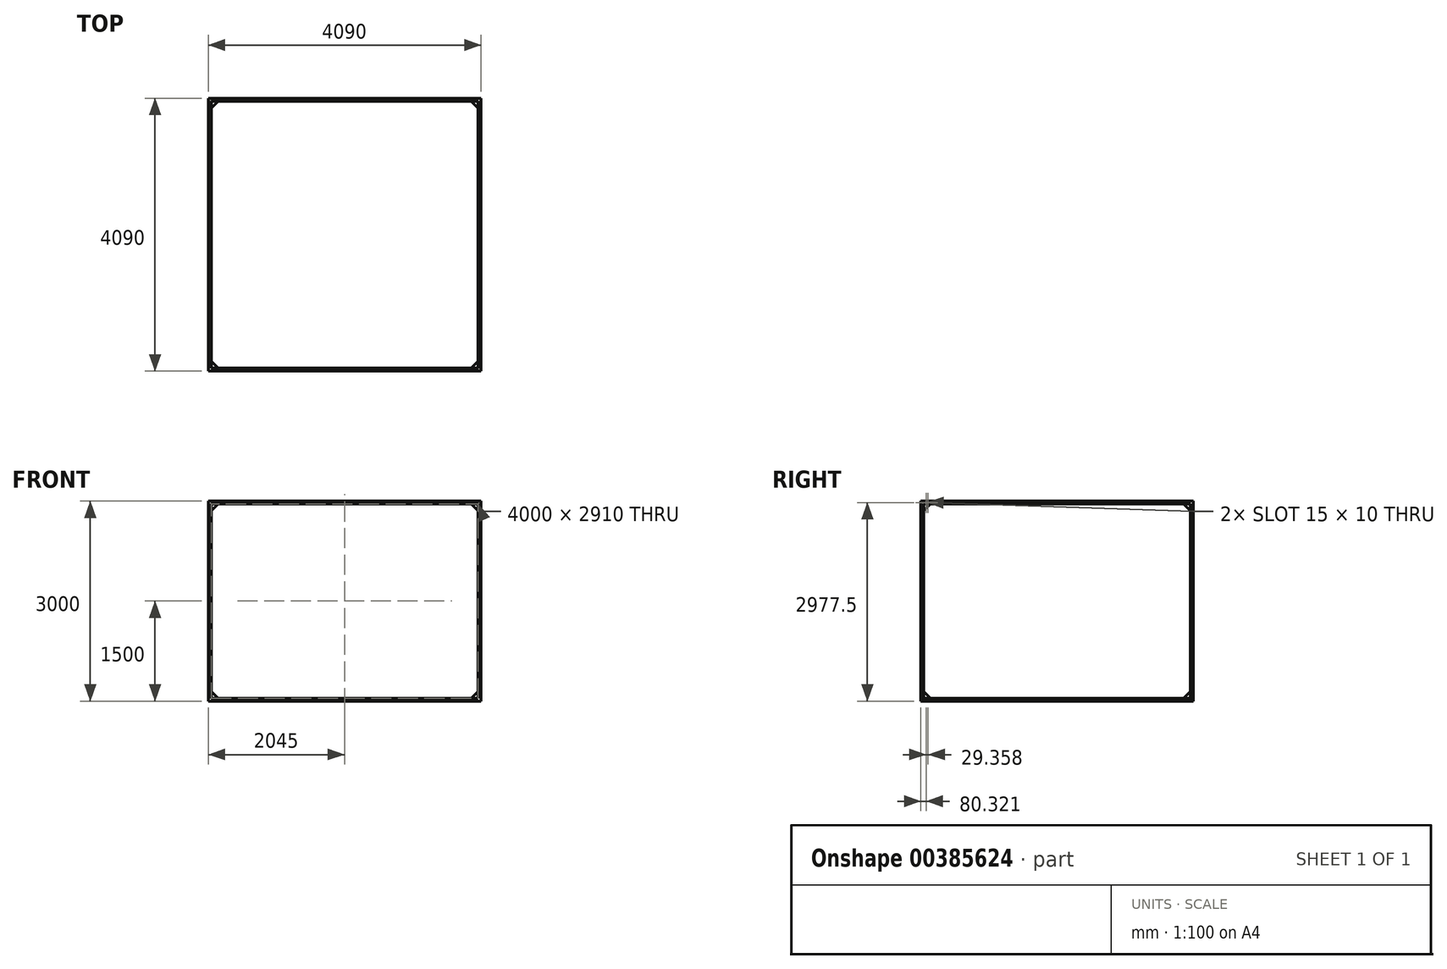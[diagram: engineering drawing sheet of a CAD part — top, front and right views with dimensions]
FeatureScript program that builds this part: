
annotation { "Feature Type Name" : "Feature", "Feature Type Description" : "" }
export const myFeature = defineFeature(function(context is Context, id is Id, definition is map)
    precondition{}
    {
        {
            var Q0;
            Q0=qCreatedBy(makeId("Front.planeOp"),FACE);
            var sketch = newSketch(context, id + "F0", { "sketchPlane" : qUnion([Q0])});
            skLineSegment(sketch, "E0.bottom", {"start": v(-214.64, 1461.4) * mm, "end": v(-169.64, 1461.4) * mm});
            skLineSegment(sketch, "E0.top", {"start": v(-214.64, -1538.6) * mm, "end": v(-169.64, -1538.6) * mm});
            skLineSegment(sketch, "E0.left", {"start": v(-214.64, 1461.4) * mm, "end": v(-214.64, -1538.6) * mm});
            skLineSegment(sketch, "E0.right", {"start": v(-169.64, 1461.4) * mm, "end": v(-169.64, -1538.6) * mm});
            skLineSegment(sketch, "E1", {"start": v(1830.36, 1828.03) * mm, "end": v(1830.36, -2580.42) * mm, "construction": true});
            skLineSegment(sketch, "E2.MirrorCS", {"start": v(3830.36, 1461.4) * mm, "end": v(3830.36, -1538.6) * mm});
            skLineSegment(sketch, "E3.MirrorCS", {"start": v(3875.36, 1461.4) * mm, "end": v(3875.36, -1538.6) * mm});
            skLineSegment(sketch, "E4.MirrorCS", {"start": v(3875.36, 1461.4) * mm, "end": v(3830.36, 1461.4) * mm});
            skLineSegment(sketch, "E5.MirrorCS", {"start": v(3875.36, -1538.6) * mm, "end": v(3830.36, -1538.6) * mm});
            skLineSegment(sketch, "E6.bottom", {"start": v(-169.64, 1461.4) * mm, "end": v(3830.36, 1461.4) * mm});
            skLineSegment(sketch, "E6.top", {"start": v(-169.64, 1416.4) * mm, "end": v(3830.36, 1416.4) * mm});
            skLineSegment(sketch, "E6.left", {"start": v(-169.64, 1461.4) * mm, "end": v(-169.64, 1416.4) * mm});
            skLineSegment(sketch, "E6.right", {"start": v(3830.36, 1461.4) * mm, "end": v(3830.36, 1416.4) * mm});
            skLineSegment(sketch, "E7.bottom", {"start": v(-169.64, -1538.6) * mm, "end": v(3830.36, -1538.6) * mm});
            skLineSegment(sketch, "E7.top", {"start": v(-169.64, -1493.6) * mm, "end": v(3830.36, -1493.6) * mm});
            skLineSegment(sketch, "E7.left", {"start": v(-169.64, -1538.6) * mm, "end": v(-169.64, -1493.6) * mm});
            skLineSegment(sketch, "E7.right", {"start": v(3830.36, -1538.6) * mm, "end": v(3830.36, -1493.6) * mm});
            skSolve(sketch);
        }
        {
            var Q0;
            {var subQ4=sQuery(id+"F0.wireOp",EDGE,"E0.bottom");Q0=makeQuery(id+"F0.imprint","IMPRINT",FACE,{"disambiguationData":[TD([[makeQuery(id+"F0.imprint","IMPRINT",EDGE,{"derivedFrom":subQ4}),-1.0]])]});}
            var Q1;
            Q1=makeQuery(id+"F0.imprint","IMPRINT",FACE,{"disambiguationData":[TD([[makeQuery(id+"F0.imprint","IMPRINT",EDGE,{"derivedFrom":sQuery(id+"F0.wireOp",EDGE,"E3.MirrorCS")}),-1.0]])]});
            var Q2;
            {var subQ0=sQuery(id+"F0.wireOp",EDGE,"E6.bottom");Q2=makeQuery(id+"F0.imprint","IMPRINT",FACE,{"disambiguationData":[TD([[makeQuery(id+"F0.imprint","IMPRINT",EDGE,{"derivedFrom":subQ0}),-1.0]])]});}
            var Q3;
            {var subQ0=sQuery(id+"F0.wireOp",EDGE,"E7.bottom");Q3=makeQuery(id+"F0.imprint","IMPRINT",FACE,{"disambiguationData":[TD([[makeQuery(id+"F0.imprint","IMPRINT",EDGE,{"derivedFrom":subQ0}),1.0]])]});}
            extrude(context, id + "F1", {"entities" : qUnion([Q0, Q1, Q2, Q3]), "depth" : 45 * mm});
        }
        {
            var Q0;
            Q0=makeQuery(id+"F1.opExtrude","CAP_FACE",FACE,{"disambiguationData":[OSD([sQuery(id+"F0.wireOp",EDGE,"E0.bottom"),sQuery(id+"F0.wireOp",EDGE,"E0.top"),sQuery(id+"F0.wireOp",EDGE,"E0.left"),sQuery(id+"F0.wireOp",EDGE,"E0.right"),sQuery(id+"F0.wireOp",EDGE,"E2.MirrorCS"),sQuery(id+"F0.wireOp",EDGE,"E3.MirrorCS"),sQuery(id+"F0.wireOp",EDGE,"E4.MirrorCS"),sQuery(id+"F0.wireOp",EDGE,"E5.MirrorCS"),sQuery(id+"F0.wireOp",EDGE,"E6.bottom"),sQuery(id+"F0.wireOp",EDGE,"E6.top"),sQuery(id+"F0.wireOp",EDGE,"E7.bottom"),sQuery(id+"F0.wireOp",EDGE,"E7.top")])],"isStart":false});
            cPlane(context, id + "F2", {"entities" : qUnion([Q0]), "cplaneType" : CPlaneType.OFFSET, "offset" : 2000 * mm, "width" : 150 * mm, "height" : 150 * mm});
        }
        {
            var Q0;
            Q0=makeQuery(id+"F1.opExtrude","SWEPT_BODY",BODY,{"disambiguationData":[OSD([sQuery(id+"F0.wireOp",EDGE,"E0.bottom"),sQuery(id+"F0.wireOp",EDGE,"E0.top"),sQuery(id+"F0.wireOp",EDGE,"E0.left"),sQuery(id+"F0.wireOp",EDGE,"E0.right"),sQuery(id+"F0.wireOp",EDGE,"E2.MirrorCS"),sQuery(id+"F0.wireOp",EDGE,"E3.MirrorCS"),sQuery(id+"F0.wireOp",EDGE,"E4.MirrorCS"),sQuery(id+"F0.wireOp",EDGE,"E5.MirrorCS"),sQuery(id+"F0.wireOp",EDGE,"E6.bottom"),sQuery(id+"F0.wireOp",EDGE,"E6.top"),sQuery(id+"F0.wireOp",EDGE,"E7.bottom"),sQuery(id+"F0.wireOp",EDGE,"E7.top")])]});
            var Q1;
            Q1=qCreatedBy(id+"F2.planeOp",FACE);
            mirror(context, id + "F3", {"entities" : qUnion([Q0]), "mirrorPlane" : qUnion([Q1])});
        }
        {
            var Q0;
            Q0=makeQuery(id+"F3.opPattern","COPY",FACE,{"derivedFrom":makeQuery(id+"F1.opExtrude","SWEPT_FACE",FACE,{"disambiguationData":[OSD([sQuery(id+"F0.wireOp",EDGE,"E0.bottom"),sQuery(id+"F0.wireOp",EDGE,"E4.MirrorCS"),sQuery(id+"F0.wireOp",EDGE,"E6.bottom")])]}),"instanceName":"1"});
            var sketch = newSketch(context, id + "F4", { "sketchPlane" : qUnion([Q0])});
            skLineSegment(sketch, "E8.bottom", {"start": v(-214.64, -4045) * mm, "end": v(-169.64, -4045) * mm});
            skLineSegment(sketch, "E8.top", {"start": v(-214.64, -45) * mm, "end": v(-169.64, -45) * mm});
            skLineSegment(sketch, "E8.left", {"start": v(-214.64, -4045) * mm, "end": v(-214.64, -45) * mm});
            skLineSegment(sketch, "E8.right", {"start": v(-169.64, -4045) * mm, "end": v(-169.64, -45) * mm});
            skLineSegment(sketch, "E9.0.0", {"start": v(3875.36, 0) * mm, "end": v(-214.64, 0) * mm});
            skLineSegment(sketch, "E9.0.1", {"start": v(-214.64, 0) * mm, "end": v(-214.64, -45) * mm});
            skLineSegment(sketch, "E9.0.2", {"start": v(-214.64, -45) * mm, "end": v(3875.36, -45) * mm});
            skLineSegment(sketch, "E9.0.3", {"start": v(3875.36, -45) * mm, "end": v(3875.36, 0) * mm});
            skLineSegment(sketch, "E10", {"start": v(1830.36, -4045) * mm, "end": v(1830.36, 1032.85) * mm, "construction": true});
            skLineSegment(sketch, "E11.MirrorCS", {"start": v(3830.36, -4045) * mm, "end": v(3830.36, -45) * mm});
            skLineSegment(sketch, "E12.MirrorCS", {"start": v(3875.36, -4045) * mm, "end": v(3875.36, -45) * mm});
            skSolve(sketch);
        }
        {
            var Q0;
            {var subQ2=sQuery(id+"F4.wireOp",EDGE,"E11.MirrorCS");Q0=makeQuery(id+"F4.imprint","IMPRINT",FACE,{"disambiguationData":[TD([[makeQuery(id+"F4.imprint","IMPRINT",EDGE,{"derivedFrom":subQ2}),-1.0]])]});}
            var Q1;
            Q1=makeQuery(id+"F4.imprint","IMPRINT",FACE,{"disambiguationData":[TD([[makeQuery(id+"F4.imprint","IMPRINT",EDGE,{"derivedFrom":sQuery(id+"F4.wireOp",EDGE,"E8.bottom")}),1.0]])]});
            extrude(context, id + "F5", {"entities" : qUnion([Q0, Q1]), "operationType" : NewBodyOperationType.ADD, "oppositeDirection" : true, "depth" : 45 * mm});
        }
        {
            var Q0;
            {var subQ0=makeQuery(id+"F1.opExtrude","SWEPT_FACE",FACE,{"disambiguationData":[OSD([sQuery(id+"F0.wireOp",EDGE,"E0.left")])]});Q0=makeQuery(id+"F5.boolean.opBoolean","MERGE",FACE,{"derivedFrom":[subQ0,makeQuery(id+"F3.opPattern","COPY",FACE,{"derivedFrom":subQ0,"instanceName":"1"}),makeQuery(id+"F5.opExtrude","SWEPT_FACE",FACE,{"disambiguationData":[OSD([sQuery(id+"F4.wireOp",EDGE,"E8.left")])]})]});}
            var sketch = newSketch(context, id + "F6", { "sketchPlane" : qUnion([Q0])});
            skLineSegment(sketch, "E13.0.0", {"start": v(0, 1461.4) * mm, "end": v(0, -1538.6) * mm});
            skLineSegment(sketch, "E13.0.1", {"start": v(0, -1538.6) * mm, "end": v(45, -1538.6) * mm});
            skLineSegment(sketch, "E13.0.2", {"start": v(45, -1538.6) * mm, "end": v(45, 1416.4) * mm});
            skLineSegment(sketch, "E13.0.3", {"start": v(45, 1416.4) * mm, "end": v(4045, 1416.4) * mm});
            skLineSegment(sketch, "E13.0.4", {"start": v(4045, 1416.4) * mm, "end": v(4045, -1538.6) * mm});
            skLineSegment(sketch, "E13.0.5", {"start": v(4045, -1538.6) * mm, "end": v(4090, -1538.6) * mm});
            skLineSegment(sketch, "E13.0.6", {"start": v(4090, -1538.6) * mm, "end": v(4090, 1461.4) * mm});
            skLineSegment(sketch, "E13.0.7", {"start": v(4090, 1461.4) * mm, "end": v(0, 1461.4) * mm});
            skLineSegment(sketch, "E14.bottom", {"start": v(4045, -1538.6) * mm, "end": v(45, -1538.6) * mm});
            skLineSegment(sketch, "E14.top", {"start": v(4045, -1493.6) * mm, "end": v(45, -1493.6) * mm});
            skLineSegment(sketch, "E14.left", {"start": v(4045, -1538.6) * mm, "end": v(4045, -1493.6) * mm});
            skLineSegment(sketch, "E14.right", {"start": v(45, -1538.6) * mm, "end": v(45, -1493.6) * mm});
            skSolve(sketch);
        }
        {
            var Q0;
            {var subQ0=sQuery(id+"F6.wireOp",EDGE,"E14.bottom");Q0=makeQuery(id+"F6.imprint","IMPRINT",FACE,{"disambiguationData":[TD([[makeQuery(id+"F6.imprint","IMPRINT",EDGE,{"derivedFrom":subQ0}),-1.0]])]});}
            extrude(context, id + "F7", {"entities" : qUnion([Q0]), "operationType" : NewBodyOperationType.ADD, "oppositeDirection" : true, "depth" : 45 * mm});
        }
        {
            var Q0;
            {var subQ0=makeQuery(id+"F1.opExtrude","SWEPT_FACE",FACE,{"disambiguationData":[OSD([sQuery(id+"F0.wireOp",EDGE,"E3.MirrorCS")])]});Q0=makeQuery(id+"F5.boolean.opBoolean","MERGE",FACE,{"derivedFrom":[subQ0,makeQuery(id+"F3.opPattern","COPY",FACE,{"derivedFrom":subQ0,"instanceName":"1"}),makeQuery(id+"F5.opExtrude","SWEPT_FACE",FACE,{"disambiguationData":[OSD([sQuery(id+"F4.wireOp",EDGE,"E12.MirrorCS")])]})]});}
            var sketch = newSketch(context, id + "F8", { "sketchPlane" : qUnion([Q0])});
            skLineSegment(sketch, "E15.0.0", {"start": v(0, -1538.6) * mm, "end": v(0, 1461.4) * mm});
            skLineSegment(sketch, "E15.0.1", {"start": v(0, 1461.4) * mm, "end": v(-4090, 1461.4) * mm});
            skLineSegment(sketch, "E15.0.2", {"start": v(-4090, 1461.4) * mm, "end": v(-4090, -1538.6) * mm});
            skLineSegment(sketch, "E15.0.3", {"start": v(-4090, -1538.6) * mm, "end": v(-4045, -1538.6) * mm});
            skLineSegment(sketch, "E15.0.4", {"start": v(-4045, -1538.6) * mm, "end": v(-4045, 1416.4) * mm});
            skLineSegment(sketch, "E15.0.5", {"start": v(-4045, 1416.4) * mm, "end": v(-45, 1416.4) * mm});
            skLineSegment(sketch, "E15.0.6", {"start": v(-45, 1416.4) * mm, "end": v(-45, -1538.6) * mm});
            skLineSegment(sketch, "E15.0.7", {"start": v(-45, -1538.6) * mm, "end": v(0, -1538.6) * mm});
            skLineSegment(sketch, "E16", {"start": v(-4045, 1416.4) * mm, "end": v(-4045, 1316.4) * mm});
            skLineSegment(sketch, "E17", {"start": v(-4045, 1316.4) * mm, "end": v(-3945, 1416.4) * mm});
            skLineSegment(sketch, "E18", {"start": v(-3945, 1416.4) * mm, "end": v(-4045, 1416.4) * mm});
            skSolve(sketch);
        }
        {
            var Q0;
            {var subQ3=sQuery(id+"F8.wireOp",EDGE,"E17");Q0=makeQuery(id+"F8.imprint","IMPRINT",FACE,{"disambiguationData":[TD([[makeQuery(id+"F8.imprint","IMPRINT",EDGE,{"derivedFrom":subQ3}),1.0]])]});}
            extrude(context, id + "F9", {"entities" : qUnion([Q0]), "oppositeDirection" : true, "depth" : 45 * mm});
        }
        {
            var Q0;
            Q0=makeQuery(id+"F9.opExtrude","SWEPT_BODY",BODY,{"disambiguationData":[OSD([sQuery(id+"F8.wireOp",EDGE,"E15.0.4"),sQuery(id+"F8.wireOp",EDGE,"E15.0.5"),sQuery(id+"F8.wireOp",EDGE,"E17")])]});
            var Q1;
            Q1=qCreatedBy(id+"F2.planeOp",FACE);
            mirror(context, id + "F10", {"entities" : qUnion([Q0]), "mirrorPlane" : qUnion([Q1])});
        }
        {
            var Q0;
            Q0=makeQuery(id+"F5.opExtrude","SWEPT_FACE",FACE,{"disambiguationData":[OSD([sQuery(id+"F4.wireOp",EDGE,"E11.MirrorCS")])]});
            cPlane(context, id + "F11", {"entities" : qUnion([Q0]), "cplaneType" : CPlaneType.OFFSET, "offset" : 2000 * mm, "width" : 150 * mm, "height" : 150 * mm});
        }
        {
            var Q0;
            Q0=makeQuery(id+"F9.opExtrude","SWEPT_BODY",BODY,{"disambiguationData":[OSD([sQuery(id+"F8.wireOp",EDGE,"E15.0.4"),sQuery(id+"F8.wireOp",EDGE,"E15.0.5"),sQuery(id+"F8.wireOp",EDGE,"E17")])]});
            var Q1;
            Q1=makeQuery(id+"F10.opPattern","COPY",BODY,{"derivedFrom":makeQuery(id+"F9.opExtrude","SWEPT_BODY",BODY,{"disambiguationData":[OSD([sQuery(id+"F8.wireOp",EDGE,"E15.0.4"),sQuery(id+"F8.wireOp",EDGE,"E15.0.5"),sQuery(id+"F8.wireOp",EDGE,"E17")])]}),"instanceName":"1"});
            var Q2;
            Q2=qCreatedBy(id+"F11.planeOp",FACE);
            mirror(context, id + "F12", {"entities" : qUnion([Q0, Q1]), "mirrorPlane" : qUnion([Q2])});
        }
        {
            var Q0;
            Q0=makeQuery(id+"F1.opExtrude","CAP_FACE",FACE,{"disambiguationData":[OSD([sQuery(id+"F0.wireOp",EDGE,"E0.bottom"),sQuery(id+"F0.wireOp",EDGE,"E0.top"),sQuery(id+"F0.wireOp",EDGE,"E0.left"),sQuery(id+"F0.wireOp",EDGE,"E0.right"),sQuery(id+"F0.wireOp",EDGE,"E2.MirrorCS"),sQuery(id+"F0.wireOp",EDGE,"E3.MirrorCS"),sQuery(id+"F0.wireOp",EDGE,"E4.MirrorCS"),sQuery(id+"F0.wireOp",EDGE,"E5.MirrorCS"),sQuery(id+"F0.wireOp",EDGE,"E6.bottom"),sQuery(id+"F0.wireOp",EDGE,"E6.top"),sQuery(id+"F0.wireOp",EDGE,"E7.bottom"),sQuery(id+"F0.wireOp",EDGE,"E7.top")])],"isStart":true});
            var sketch = newSketch(context, id + "F13", { "sketchPlane" : qUnion([Q0])});
            skLineSegment(sketch, "E19", {"start": v(-3830.36, 1416.4) * mm, "end": v(-3830.36, 1316.4) * mm});
            skLineSegment(sketch, "E20", {"start": v(-3830.36, 1316.4) * mm, "end": v(-3730.36, 1416.4) * mm});
            skLineSegment(sketch, "E21", {"start": v(-3730.36, 1416.4) * mm, "end": v(-3830.36, 1416.4) * mm});
            skSolve(sketch);
        }
        {
            var Q0;
            Q0=makeQuery(id+"F13.imprint","IMPRINT",FACE,{"disambiguationData":[TD([[makeQuery(id+"F13.imprint","IMPRINT",EDGE,{"derivedFrom":sQuery(id+"F13.wireOp",EDGE,"E19")}),1.0]])]});
            extrude(context, id + "F14", {"entities" : qUnion([Q0]), "oppositeDirection" : true, "depth" : 45 * mm});
        }
        {
            var Q0;
            Q0=makeQuery(id+"F14.opExtrude","SWEPT_BODY",BODY,{"disambiguationData":[OSD([sQuery(id+"F13.wireOp",EDGE,"E19"),sQuery(id+"F13.wireOp",EDGE,"E20"),sQuery(id+"F13.wireOp",EDGE,"E21")])]});
            var Q1;
            Q1=qCreatedBy(id+"F11.planeOp",FACE);
            mirror(context, id + "F15", {"entities" : qUnion([Q0]), "mirrorPlane" : qUnion([Q1])});
        }
        {
            var Q0;
            Q0=makeQuery(id+"F14.opExtrude","SWEPT_BODY",BODY,{"disambiguationData":[OSD([sQuery(id+"F13.wireOp",EDGE,"E19"),sQuery(id+"F13.wireOp",EDGE,"E20"),sQuery(id+"F13.wireOp",EDGE,"E21")])]});
            var Q1;
            Q1=makeQuery(id+"F15.opPattern","COPY",BODY,{"derivedFrom":makeQuery(id+"F14.opExtrude","SWEPT_BODY",BODY,{"disambiguationData":[OSD([sQuery(id+"F13.wireOp",EDGE,"E19"),sQuery(id+"F13.wireOp",EDGE,"E20"),sQuery(id+"F13.wireOp",EDGE,"E21")])]}),"instanceName":"1"});
            var Q2;
            Q2=qCreatedBy(id+"F2.planeOp",FACE);
            mirror(context, id + "F16", {"entities" : qUnion([Q0, Q1]), "mirrorPlane" : qUnion([Q2])});
        }
        {
            var Q0;
            {var subQ0=sQuery(id+"F0.wireOp",EDGE,"E6.bottom");var subQ1=sQuery(id+"F0.wireOp",EDGE,"E4.MirrorCS");var subQ2=sQuery(id+"F0.wireOp",EDGE,"E0.bottom");var subQ3=makeQuery(id+"F1.opExtrude","SWEPT_FACE",FACE,{"disambiguationData":[OSD([subQ2,subQ1,subQ0])]});Q0=makeQuery(id+"F5.boolean.opBoolean","MERGE",FACE,{"derivedFrom":[subQ3,makeQuery(id+"F3.opPattern","COPY",FACE,{"derivedFrom":subQ3,"instanceName":"1"}),makeQuery(id+"F5.opExtrude","CAP_FACE",FACE,{"disambiguationData":[OSD([sQuery(id+"F4.wireOp",EDGE,"E8.bottom"),sQuery(id+"F4.wireOp",EDGE,"E8.top"),sQuery(id+"F4.wireOp",EDGE,"E8.left"),sQuery(id+"F4.wireOp",EDGE,"E8.right")])],"isStart":true}),makeQuery(id+"F5.opExtrude","CAP_FACE",FACE,{"disambiguationData":[OSD([subQ2,subQ1,subQ0,sQuery(id+"F4.wireOp",EDGE,"E9.0.2"),sQuery(id+"F4.wireOp",EDGE,"E11.MirrorCS"),sQuery(id+"F4.wireOp",EDGE,"E12.MirrorCS")])],"isStart":true})]});}
            var sketch = newSketch(context, id + "F17", { "sketchPlane" : qUnion([Q0])});
            skLineSegment(sketch, "E22", {"start": v(-169.64, -4045) * mm, "end": v(-169.64, -3945) * mm});
            skLineSegment(sketch, "E23", {"start": v(-169.64, -3945) * mm, "end": v(-69.64, -4045) * mm});
            skLineSegment(sketch, "E24", {"start": v(-69.64, -4045) * mm, "end": v(-169.64, -4045) * mm});
            skSolve(sketch);
        }
        {
            var Q0;
            Q0=makeQuery(id+"F17.imprint","IMPRINT",FACE,{"disambiguationData":[TD([[makeQuery(id+"F17.imprint","IMPRINT",EDGE,{"derivedFrom":sQuery(id+"F17.wireOp",EDGE,"E22")}),-1.0]])]});
            extrude(context, id + "F18", {"entities" : qUnion([Q0]), "oppositeDirection" : true, "depth" : 45 * mm});
        }
        {
            var Q0;
            Q0=makeQuery(id+"F18.opExtrude","SWEPT_BODY",BODY,{"disambiguationData":[OSD([sQuery(id+"F17.wireOp",EDGE,"E22"),sQuery(id+"F17.wireOp",EDGE,"E23"),sQuery(id+"F17.wireOp",EDGE,"E24")])]});
            var Q1;
            Q1=qCreatedBy(id+"F11.planeOp",FACE);
            mirror(context, id + "F19", {"entities" : qUnion([Q0]), "mirrorPlane" : qUnion([Q1])});
        }
        {
            var Q0;
            Q0=makeQuery(id+"F18.opExtrude","SWEPT_BODY",BODY,{"disambiguationData":[OSD([sQuery(id+"F17.wireOp",EDGE,"E22"),sQuery(id+"F17.wireOp",EDGE,"E23"),sQuery(id+"F17.wireOp",EDGE,"E24")])]});
            var Q1;
            Q1=makeQuery(id+"F19.opPattern","COPY",BODY,{"derivedFrom":makeQuery(id+"F18.opExtrude","SWEPT_BODY",BODY,{"disambiguationData":[OSD([sQuery(id+"F17.wireOp",EDGE,"E22"),sQuery(id+"F17.wireOp",EDGE,"E23"),sQuery(id+"F17.wireOp",EDGE,"E24")])]}),"instanceName":"1"});
            var Q2;
            Q2=qCreatedBy(id+"F2.planeOp",FACE);
            mirror(context, id + "F20", {"entities" : qUnion([Q0, Q1]), "mirrorPlane" : qUnion([Q2])});
        }
        {
            var Q0;
            Q0=makeQuery(id+"F1.opExtrude","SWEPT_FACE",FACE,{"disambiguationData":[OSD([sQuery(id+"F0.wireOp",EDGE,"E6.top")])]});
            cPlane(context, id + "F21", {"entities" : qUnion([Q0]), "cplaneType" : CPlaneType.OFFSET, "offset" : 1500 * mm - 45 * mm, "width" : 150 * mm, "height" : 150 * mm});
        }
        {
            var Q0;
            Q0=makeQuery(id+"F14.opExtrude","SWEPT_BODY",BODY,{"disambiguationData":[OSD([sQuery(id+"F13.wireOp",EDGE,"E19"),sQuery(id+"F13.wireOp",EDGE,"E20"),sQuery(id+"F13.wireOp",EDGE,"E21")])]});
            var Q1;
            Q1=makeQuery(id+"F15.opPattern","COPY",BODY,{"derivedFrom":makeQuery(id+"F14.opExtrude","SWEPT_BODY",BODY,{"disambiguationData":[OSD([sQuery(id+"F13.wireOp",EDGE,"E19"),sQuery(id+"F13.wireOp",EDGE,"E20"),sQuery(id+"F13.wireOp",EDGE,"E21")])]}),"instanceName":"1"});
            var Q2;
            Q2=makeQuery(id+"F16.opPattern","COPY",BODY,{"derivedFrom":makeQuery(id+"F14.opExtrude","SWEPT_BODY",BODY,{"disambiguationData":[OSD([sQuery(id+"F13.wireOp",EDGE,"E19"),sQuery(id+"F13.wireOp",EDGE,"E20"),sQuery(id+"F13.wireOp",EDGE,"E21")])]}),"instanceName":"1"});
            var Q3;
            Q3=makeQuery(id+"F16.opPattern","COPY",BODY,{"derivedFrom":makeQuery(id+"F15.opPattern","COPY",BODY,{"derivedFrom":makeQuery(id+"F14.opExtrude","SWEPT_BODY",BODY,{"disambiguationData":[OSD([sQuery(id+"F13.wireOp",EDGE,"E19"),sQuery(id+"F13.wireOp",EDGE,"E20"),sQuery(id+"F13.wireOp",EDGE,"E21")])]}),"instanceName":"1"}),"instanceName":"1"});
            var Q4;
            Q4=makeQuery(id+"F12.opPattern","COPY",BODY,{"derivedFrom":makeQuery(id+"F10.opPattern","COPY",BODY,{"derivedFrom":makeQuery(id+"F9.opExtrude","SWEPT_BODY",BODY,{"disambiguationData":[OSD([sQuery(id+"F8.wireOp",EDGE,"E15.0.4"),sQuery(id+"F8.wireOp",EDGE,"E15.0.5"),sQuery(id+"F8.wireOp",EDGE,"E17")])]}),"instanceName":"1"}),"instanceName":"1"});
            var Q5;
            Q5=makeQuery(id+"F12.opPattern","COPY",BODY,{"derivedFrom":makeQuery(id+"F9.opExtrude","SWEPT_BODY",BODY,{"disambiguationData":[OSD([sQuery(id+"F8.wireOp",EDGE,"E15.0.4"),sQuery(id+"F8.wireOp",EDGE,"E15.0.5"),sQuery(id+"F8.wireOp",EDGE,"E17")])]}),"instanceName":"1"});
            var Q6;
            Q6=makeQuery(id+"F20.opPattern","COPY",BODY,{"derivedFrom":makeQuery(id+"F18.opExtrude","SWEPT_BODY",BODY,{"disambiguationData":[OSD([sQuery(id+"F17.wireOp",EDGE,"E22"),sQuery(id+"F17.wireOp",EDGE,"E23"),sQuery(id+"F17.wireOp",EDGE,"E24")])]}),"instanceName":"1"});
            var Q7;
            Q7=makeQuery(id+"F18.opExtrude","SWEPT_BODY",BODY,{"disambiguationData":[OSD([sQuery(id+"F17.wireOp",EDGE,"E22"),sQuery(id+"F17.wireOp",EDGE,"E23"),sQuery(id+"F17.wireOp",EDGE,"E24")])]});
            var Q8;
            Q8=qCreatedBy(id+"F21.planeOp",FACE);
            mirror(context, id + "F22", {"entities" : qUnion([Q0, Q1, Q2, Q3, Q4, Q5, Q6, Q7]), "mirrorPlane" : qUnion([Q8])});
        }
        {
            var Q0;
            Q0=makeQuery(id+"F22.opPattern","COPY",FACE,{"derivedFrom":makeQuery(id+"F12.opPattern","COPY",FACE,{"derivedFrom":makeQuery(id+"F10.opPattern","COPY",FACE,{"derivedFrom":makeQuery(id+"F9.opExtrude","SWEPT_FACE",FACE,{"disambiguationData":[OSD([sQuery(id+"F8.wireOp",EDGE,"E17")])]}),"instanceName":"1"}),"instanceName":"1"}),"instanceName":"1"});
            var Q1;
            Q1=makeQuery(id+"F22.opPattern","COPY",FACE,{"derivedFrom":makeQuery(id+"F15.opPattern","COPY",FACE,{"derivedFrom":makeQuery(id+"F14.opExtrude","SWEPT_FACE",FACE,{"disambiguationData":[OSD([sQuery(id+"F13.wireOp",EDGE,"E20")])]}),"instanceName":"1"}),"instanceName":"1"});
            var Q2;
            Q2=makeQuery(id+"F22.opPattern","COPY",FACE,{"derivedFrom":makeQuery(id+"F20.opPattern","COPY",FACE,{"derivedFrom":makeQuery(id+"F18.opExtrude","SWEPT_FACE",FACE,{"disambiguationData":[OSD([sQuery(id+"F17.wireOp",EDGE,"E23")])]}),"instanceName":"1"}),"instanceName":"1"});
            var Q3;
            Q3=makeQuery(id+"F20.opPattern","COPY",FACE,{"derivedFrom":makeQuery(id+"F18.opExtrude","SWEPT_FACE",FACE,{"disambiguationData":[OSD([sQuery(id+"F17.wireOp",EDGE,"E23")])]}),"instanceName":"1"});
            var Q4;
            Q4=makeQuery(id+"F12.opPattern","COPY",FACE,{"derivedFrom":makeQuery(id+"F10.opPattern","COPY",FACE,{"derivedFrom":makeQuery(id+"F9.opExtrude","SWEPT_FACE",FACE,{"disambiguationData":[OSD([sQuery(id+"F8.wireOp",EDGE,"E17")])]}),"instanceName":"1"}),"instanceName":"1"});
            var Q5;
            Q5=makeQuery(id+"F15.opPattern","COPY",FACE,{"derivedFrom":makeQuery(id+"F14.opExtrude","SWEPT_FACE",FACE,{"disambiguationData":[OSD([sQuery(id+"F13.wireOp",EDGE,"E20")])]}),"instanceName":"1"});
            var Q6;
            Q6=makeQuery(id+"F20.opPattern","COPY",FACE,{"derivedFrom":makeQuery(id+"F19.opPattern","COPY",FACE,{"derivedFrom":makeQuery(id+"F18.opExtrude","SWEPT_FACE",FACE,{"disambiguationData":[OSD([sQuery(id+"F17.wireOp",EDGE,"E23")])]}),"instanceName":"1"}),"instanceName":"1"});
            var Q7;
            Q7=makeQuery(id+"F10.opPattern","COPY",FACE,{"derivedFrom":makeQuery(id+"F9.opExtrude","SWEPT_FACE",FACE,{"disambiguationData":[OSD([sQuery(id+"F8.wireOp",EDGE,"E17")])]}),"instanceName":"1"});
            var Q8;
            Q8=makeQuery(id+"F14.opExtrude","SWEPT_FACE",FACE,{"disambiguationData":[OSD([sQuery(id+"F13.wireOp",EDGE,"E20")])]});
            var Q9;
            Q9=makeQuery(id+"F19.opPattern","COPY",FACE,{"derivedFrom":makeQuery(id+"F18.opExtrude","SWEPT_FACE",FACE,{"disambiguationData":[OSD([sQuery(id+"F17.wireOp",EDGE,"E23")])]}),"instanceName":"1"});
            var Q10;
            Q10=makeQuery(id+"F9.opExtrude","SWEPT_FACE",FACE,{"disambiguationData":[OSD([sQuery(id+"F8.wireOp",EDGE,"E17")])]});
            var Q11;
            Q11=makeQuery(id+"F16.opPattern","COPY",FACE,{"derivedFrom":makeQuery(id+"F14.opExtrude","SWEPT_FACE",FACE,{"disambiguationData":[OSD([sQuery(id+"F13.wireOp",EDGE,"E20")])]}),"instanceName":"1"});
            var Q12;
            Q12=makeQuery(id+"F18.opExtrude","SWEPT_FACE",FACE,{"disambiguationData":[OSD([sQuery(id+"F17.wireOp",EDGE,"E23")])]});
            var Q13;
            Q13=makeQuery(id+"F16.opPattern","COPY",FACE,{"derivedFrom":makeQuery(id+"F15.opPattern","COPY",FACE,{"derivedFrom":makeQuery(id+"F14.opExtrude","SWEPT_FACE",FACE,{"disambiguationData":[OSD([sQuery(id+"F13.wireOp",EDGE,"E20")])]}),"instanceName":"1"}),"instanceName":"1"});
            var Q14;
            Q14=makeQuery(id+"F12.opPattern","COPY",FACE,{"derivedFrom":makeQuery(id+"F9.opExtrude","SWEPT_FACE",FACE,{"disambiguationData":[OSD([sQuery(id+"F8.wireOp",EDGE,"E17")])]}),"instanceName":"1"});
            var Q15;
            Q15=makeQuery(id+"F22.opPattern","COPY",FACE,{"derivedFrom":makeQuery(id+"F14.opExtrude","SWEPT_FACE",FACE,{"disambiguationData":[OSD([sQuery(id+"F13.wireOp",EDGE,"E20")])]}),"instanceName":"1"});
            var Q16;
            Q16=makeQuery(id+"F22.opPattern","COPY",FACE,{"derivedFrom":makeQuery(id+"F16.opPattern","COPY",FACE,{"derivedFrom":makeQuery(id+"F14.opExtrude","SWEPT_FACE",FACE,{"disambiguationData":[OSD([sQuery(id+"F13.wireOp",EDGE,"E20")])]}),"instanceName":"1"}),"instanceName":"1"});
            var Q17;
            Q17=makeQuery(id+"F22.opPattern","COPY",FACE,{"derivedFrom":makeQuery(id+"F16.opPattern","COPY",FACE,{"derivedFrom":makeQuery(id+"F15.opPattern","COPY",FACE,{"derivedFrom":makeQuery(id+"F14.opExtrude","SWEPT_FACE",FACE,{"disambiguationData":[OSD([sQuery(id+"F13.wireOp",EDGE,"E20")])]}),"instanceName":"1"}),"instanceName":"1"}),"instanceName":"1"});
            var Q18;
            Q18=makeQuery(id+"F22.opPattern","COPY",FACE,{"derivedFrom":makeQuery(id+"F18.opExtrude","SWEPT_FACE",FACE,{"disambiguationData":[OSD([sQuery(id+"F17.wireOp",EDGE,"E23")])]}),"instanceName":"1"});
            var Q19;
            Q19=makeQuery(id+"F22.opPattern","COPY",FACE,{"derivedFrom":makeQuery(id+"F12.opPattern","COPY",FACE,{"derivedFrom":makeQuery(id+"F9.opExtrude","SWEPT_FACE",FACE,{"disambiguationData":[OSD([sQuery(id+"F8.wireOp",EDGE,"E17")])]}),"instanceName":"1"}),"instanceName":"1"});
            shell(context, id + "F23", {"entities" : qUnion([Q0, Q1, Q2, Q3, Q4, Q5, Q6, Q7, Q8, Q9, Q10, Q11, Q12, Q13, Q14, Q15, Q16, Q17, Q18, Q19]), "thickness" : 5 * mm});
        }
        {
            var Q0;
            {var subQ0=sQuery(id+"F17.wireOp",EDGE,"E22");Q0=makeQuery(id+"F23.opShell","OFFSET_FACE",FACE,{"disambiguationData":[OSD([subQ0]),TDD([makeQuery(id+"F19.opPattern","COPY",FACE,{"derivedFrom":makeQuery(id+"F18.opExtrude","SWEPT_FACE",FACE,{"disambiguationData":[OSD([subQ0])]}),"instanceName":"1"})])]});}
            var sketch = newSketch(context, id + "F24", { "sketchPlane" : qUnion([Q0])});
            skArc(sketch, "E25", {"start": v(3977.82, 1443.9) * mm, "mid": v(3972.82, 1438.9) * mm, "end": v(3977.82, 1433.9) * mm});
            skPoint(sketch, "E25.centerSnap0", {"position": v(3950, 1438.9) * mm});
            skArc(sketch, "E26", {"start": v(3982.82, 1433.9) * mm, "mid": v(3987.82, 1438.9) * mm, "end": v(3982.82, 1443.9) * mm});
            skLineSegment(sketch, "E27.bottom", {"start": v(3977.82, 1443.9) * mm, "end": v(3982.82, 1443.9) * mm});
            skLineSegment(sketch, "E27.top", {"start": v(3977.82, 1433.9) * mm, "end": v(3982.82, 1433.9) * mm});
            skLineSegment(sketch, "E28", {"start": v(3995, 1456.4) * mm, "end": v(3995, 1425.44) * mm, "construction": true});
            skPoint(sketch, "E28.endSnap0", {"position": v(3995, 1456.4) * mm});
            skArc(sketch, "E29.MirrorCS", {"start": v(4007.18, 1433.9) * mm, "mid": v(4002.18, 1438.9) * mm, "end": v(4007.18, 1443.9) * mm});
            skArc(sketch, "E30.MirrorCS", {"start": v(4012.18, 1443.9) * mm, "mid": v(4017.18, 1438.9) * mm, "end": v(4012.18, 1433.9) * mm});
            skLineSegment(sketch, "E31.MirrorCS", {"start": v(4012.18, 1443.9) * mm, "end": v(4007.18, 1443.9) * mm});
            skLineSegment(sketch, "E32.MirrorCS", {"start": v(4012.18, 1433.9) * mm, "end": v(4007.18, 1433.9) * mm});
            skSolve(sketch);
        }
        {
            var Q0;
            Q0 = qSketchRegion(id + "F24", true);
            extrude(context, id + "F25", {"entities" : qUnion([Q0]), "operationType" : NewBodyOperationType.REMOVE, "oppositeDirection" : true, "depth" : 25 * mm});
        }
    });
